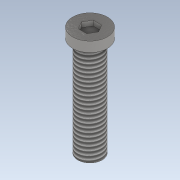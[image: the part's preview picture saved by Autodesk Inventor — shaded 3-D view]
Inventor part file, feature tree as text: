
AUTODESK INVENTOR PART (.ipt)
format: ipt  version: 2022 (Build 260153000, 153)  size: 126,464 bytes
history: native  units: mm
features: extrude x3, sketch x3, thread x1
ambient origin geometry x8: Origin, YZ Plane, XZ Plane, XY Plane, X Axis, Y Axis, Z Axis, Center Point
bodies: Solid1 (feature_tree)
feature tree (7):
  extrude  "Extrusion1"  Depth=20.0mm TaperAngle=0.0deg
  extrude  "Extrusion2"  Depth=2.0mm TaperAngle=0.0deg
  thread  "Thread1"  [1 undecoded]
  extrude  "Extrusion3"  Depth=1.0mm TaperAngle=0.0deg
  sketch  "Sketch1"  dims[d0=4.9mm d1=20.0mm d2=0.0mm]
  sketch  "Sketch2"  dims[d3=7.0mm d4=2.0mm d5=0.0mm d6=20.0mm d7=0.0mm]
  sketch  "Sketch3"  dims[d8=3.0mm d9=1.0mm d10=0.0mm]
note: 1 required parameter value undecoded (feature->parameter linkage not recoverable at this tier; creation-order binding heuristic only, values carry confidence <= 0.55)
